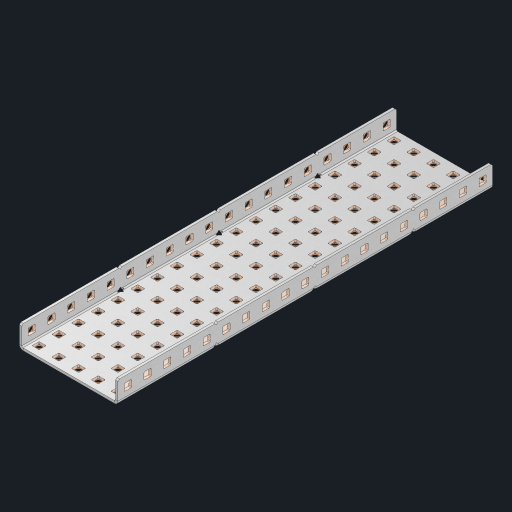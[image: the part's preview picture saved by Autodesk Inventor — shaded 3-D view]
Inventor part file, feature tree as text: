
AUTODESK INVENTOR PART (.ipt)
format: ipt  version: 2023 (Build 270158000, 158)  size: 1,603,072 bytes
history: native  units: in
note: dims shown in document units (in); Inventor stores cm internally (conversion verified against a paired STEP export)
features: other x138, extrude x132, sheet_metal_op x10, sketch x8, mirror x1, pattern_linear x1, chamfer x1
ambient origin geometry x8: Origin, YZ Plane, XZ Plane, XY Plane, X Axis, Y Axis, Z Axis, Center Point
bodies: Solid1 (feature_tree), Body (feature_tree)
feature tree (291):
  other  "Flange Pattern Plane"
  sheet_metal_op  "Flange Pattern"
  sheet_metal_op  "Body Pattern"
  other  "Arc Length"
  mirror  "Notch Mirror"
  pattern_linear  "Notch Pattern"  Spacing1=0.25in  [1 undecoded]
  chamfer  "End Chamfer"
  extrude  "Half Cut"  Depth=0.0625in
  sketch  "Sketch1"  dims[d0=2.5in]
  other  "Plate1"
  sketch  "Sketch2"  dims[d1=9.5in]
  other  "Plate2"
  sheet_metal_op  "Bend1"
  sheet_metal_op  "Corner1"
  sketch  "Sketch3"  dims[d2=0.0625in]
  other  "Flange Pattern Sketch"
  sketch  "Sketch7"  dims[d3=0.0625in]
  other  "Srf1"
  other  "Srf2"
  sketch  "Sketch8"  dims[d4=0.0312in]
  sketch  "Sketch9"  dims[d5=0.125in]
  other  "Srf91"
  sheet_metal_op  "Body Pattern Sketch"
  other  "Srf92"
  sketch  "Sketch13"  dims[d6=0.0625in]
  sketch  "Sketch14"  dims[d7=0.5in d8=90.0deg d9=0.0312in d10=0.25in d11=0.0625in d12=0.0625in d16=0.182in d17=0.02in d18=0.0625in d19=0.0in d20=0.25in d21=0.25in d46=0.172in d47=1.0in d48=0.0in d49=0.182in d50=0.02in d51=0.25in d52=0.25in d53=0.0625in d54=0.0in d55=0.172in d56=1.0in d57=0.0in d60=7.4803in d62=0.5in d63=1.9685in d65=0.5in d85=0.1473in d86=0.1782in d88=0.04in d89=0.0625in d90=0.0in d91=0.04in d92=0.0491in d95=2.5in d96=0.04in d97=0.25in d98=45.0deg d101=0.0in d102=2.497in d131=2.5in d132=7.4803in d134=0.5in d139=0.5in]
  other  "Srf856"
  other  "Srf1310"
  other  "Srf1311"
  other  "Srf1312"
  other  "Srf1376"
  other  "Srf1377"
  other  "Srf1728"
  other  "Srf1755"
  other  "Srf1878"
  other  "Srf1879"
  other  "Srf1880"
  other  "Srf1881"
  other  "Srf1882"
  other  "Srf1883"
  other  "Srf1884"
  other  "Srf1885"
  other  "Srf1886"
  other  "Srf1887"
  other  "Srf1888"
  other  "Srf1889"
  other  "Srf1890"
  other  "Srf1891"
  other  "Srf1892"
  other  "Srf1893"
  other  "Srf1894"
  other  "Srf1895"
  other  "Srf1896"
  other  "Srf1897"
  other  "Srf1898"
  other  "Srf1899"
  other  "Srf1900"
  other  "Srf1901"
  other  "Srf1902"
  other  "Srf1903"
  other  "Srf1904"
  other  "Srf1905"
  other  "Srf1906"
  other  "Srf1942"
  other  "Srf1943"
  other  "Srf1944"
  other  "Srf1945"
  other  "Srf1946"
  other  "Srf1947"
  other  "Srf1948"
  other  "Srf1949"
  other  "Srf1950"
  other  "Srf1951"
  other  "Srf1952"
  other  "Srf1953"
  other  "Srf1954"
  other  "Srf1955"
  other  "Srf1956"
  other  "Srf1957"
  other  "Srf1958"
  other  "Srf1959"
  other  "Srf1960"
  other  "Srf1961"
  other  "Srf1962"
  other  "Srf1963"
  other  "Srf1964"
  other  "Srf1965"
  other  "Srf1966"
  other  "Srf1967"
  other  "Srf1968"
  other  "Srf1969"
  other  "Srf1970"
  other  "Srf2111"
  other  "Srf2112"
  other  "Srf2113"
  other  "Srf2146"
  other  "Srf2147"
  other  "Srf2148"
  other  "Srf2149"
  other  "Srf2150"
  other  "Srf2151"
  other  "Srf2152"
  other  "Srf2153"
  other  "Srf2154"
  other  "Srf2155"
  other  "Srf2156"
  other  "Srf2157"
  other  "Srf2158"
  other  "Srf2159"
  other  "Srf2160"
  other  "Srf2161"
  other  "Srf2162"
  other  "Srf2163"
  other  "Srf2164"
  other  "Srf2165"
  other  "Srf2166"
  other  "Srf2167"
  other  "Srf2168"
  other  "Srf2169"
  other  "Srf2170"
  other  "Srf2171"
  other  "Srf2172"
  other  "Srf2173"
  other  "Srf2174"
  other  "Srf2175"
  other  "Srf2176"
  other  "Srf2177"
  other  "Srf2178"
  other  "Srf2179"
  other  "Srf2180"
  other  "Srf2181"
  other  "Srf2182"
  other  "Srf2183"
  other  "Srf2184"
  other  "Srf2185"
  other  "Srf2186"
  other  "Srf2187"
  other  "Srf2188"
  other  "Srf2189"
  other  "Srf2190"
  other  "Srf2191"
  other  "Srf2192"
  other  "Srf2193"
  other  "Srf2194"
  other  "Srf2195"
  other  "Srf2196"
  other  "Srf2197"
  other  "Srf2198"
  other  "Srf2199"
  other  "Srf2200"
  other  "Srf2201"
  other  "Srf2202"
  other  "Srf2203"
  other  "Srf2204"
  other  "Srf2205"
  sheet_metal_op  "Flange Stamp"
  sheet_metal_op  "Flange Circle"
  sheet_metal_op  "Body Stamp"
  sheet_metal_op  "Body Circle"
  sheet_metal_op  "Notch"
  extrude  "ExtrusionSrf2"  Depth=0.0625in
  extrude  "ExtrusionSrf92"  Depth=2.5in
  extrude  "ExtrusionSrf856"  Depth=0.02in
  extrude  "ExtrusionSrf1310"  Depth=0.0625in
  extrude  "ExtrusionSrf1311"  TaperAngle=0.0deg  [1 undecoded]
  extrude  "ExtrusionSrf1312"  Depth=0.25in
  extrude  "ExtrusionSrf1376"  Depth=0.25in
  extrude  "ExtrusionSrf1377"  Depth=2.5in
  extrude  "ExtrusionSrf1728"  Depth=2.5in TaperAngle=0.0deg
  extrude  "ExtrusionSrf1755"  Depth=2.5in
  extrude  "ExtrusionSrf1878"  Depth=0.02in
  extrude  "ExtrusionSrf1879"  Depth=0.25in
  extrude  "ExtrusionSrf1880"  Depth=0.25in
  extrude  "ExtrusionSrf1881"  Depth=0.0625in
  extrude  "ExtrusionSrf1882"  TaperAngle=0.0deg  [1 undecoded]
  extrude  "ExtrusionSrf1883"  Depth=2.5in
  extrude  "ExtrusionSrf1884"  Depth=2.5in TaperAngle=0.0deg
  extrude  "ExtrusionSrf1885"  Depth=2.5in
  extrude  "ExtrusionSrf1886"  Depth=2.5in
  extrude  "ExtrusionSrf1887"  Depth=2.5in
  extrude  "ExtrusionSrf1888"  Depth=2.5in
  extrude  "ExtrusionSrf1889"  Depth=2.5in
  extrude  "ExtrusionSrf1890"  Depth=0.0625in
  extrude  "ExtrusionSrf1891"  TaperAngle=0.0deg  [1 undecoded]
  extrude  "ExtrusionSrf1892"  Depth=2.5in
  extrude  "ExtrusionSrf1893"  Depth=2.5in
  extrude  "ExtrusionSrf1894"  Depth=2.5in
  extrude  "ExtrusionSrf1895"  Depth=0.25in TaperAngle=45.0deg
  extrude  "ExtrusionSrf1896"  TaperAngle=0.0deg  [1 undecoded]
  extrude  "ExtrusionSrf1897"  Depth=2.5in
  extrude  "ExtrusionSrf1898"  Depth=2.5in
  extrude  "ExtrusionSrf1899"  Depth=2.5in
  extrude  "ExtrusionSrf1900"  Depth=2.5in
  extrude  "ExtrusionSrf1901"  Depth=2.5in
  extrude  "ExtrusionSrf1902"  [1 undecoded]
  extrude  "ExtrusionSrf1903"  [1 undecoded]
  extrude  "ExtrusionSrf1904"  [1 undecoded]
  extrude  "ExtrusionSrf1905"  [1 undecoded]
  extrude  "ExtrusionSrf1906"  [1 undecoded]
  extrude  "ExtrusionSrf1942"  [1 undecoded]
  extrude  "ExtrusionSrf1943"  [1 undecoded]
  extrude  "ExtrusionSrf1944"  [1 undecoded]
  extrude  "ExtrusionSrf1945"  [1 undecoded]
  extrude  "ExtrusionSrf1946"  [1 undecoded]
  extrude  "ExtrusionSrf1947"  [1 undecoded]
  extrude  "ExtrusionSrf1948"  [1 undecoded]
  extrude  "ExtrusionSrf1949"  [1 undecoded]
  extrude  "ExtrusionSrf1950"  [1 undecoded]
  extrude  "ExtrusionSrf1951"  [1 undecoded]
  extrude  "ExtrusionSrf1952"  [1 undecoded]
  extrude  "ExtrusionSrf1953"  [1 undecoded]
  extrude  "ExtrusionSrf1954"  [1 undecoded]
  extrude  "ExtrusionSrf1955"  [1 undecoded]
  extrude  "ExtrusionSrf1956"  [1 undecoded]
  extrude  "ExtrusionSrf1957"  [1 undecoded]
  extrude  "ExtrusionSrf1958"  [1 undecoded]
  extrude  "ExtrusionSrf1959"  [1 undecoded]
  extrude  "ExtrusionSrf1960"  [1 undecoded]
  extrude  "ExtrusionSrf1961"  [1 undecoded]
  extrude  "ExtrusionSrf1962"  [1 undecoded]
  extrude  "ExtrusionSrf1963"  [1 undecoded]
  extrude  "ExtrusionSrf1964"  [1 undecoded]
  extrude  "ExtrusionSrf1965"  [1 undecoded]
  extrude  "ExtrusionSrf1966"  [1 undecoded]
  extrude  "ExtrusionSrf1967"  [1 undecoded]
  extrude  "ExtrusionSrf1968"  [1 undecoded]
  extrude  "ExtrusionSrf1969"  [1 undecoded]
  extrude  "ExtrusionSrf1970"  [1 undecoded]
  extrude  "ExtrusionSrf2111"  [1 undecoded]
  extrude  "ExtrusionSrf2112"  [1 undecoded]
  extrude  "ExtrusionSrf2113"  [1 undecoded]
  extrude  "ExtrusionSrf2146"  [1 undecoded]
  extrude  "ExtrusionSrf2147"  [1 undecoded]
  extrude  "ExtrusionSrf2148"  [1 undecoded]
  extrude  "ExtrusionSrf2149"  [1 undecoded]
  extrude  "ExtrusionSrf2150"  [1 undecoded]
  extrude  "ExtrusionSrf2151"  [1 undecoded]
  extrude  "ExtrusionSrf2152"  [1 undecoded]
  extrude  "ExtrusionSrf2153"  [1 undecoded]
  extrude  "ExtrusionSrf2154"  [1 undecoded]
  extrude  "ExtrusionSrf2155"  [1 undecoded]
  extrude  "ExtrusionSrf2156"  [1 undecoded]
  extrude  "ExtrusionSrf2157"  [1 undecoded]
  extrude  "ExtrusionSrf2158"  [1 undecoded]
  extrude  "ExtrusionSrf2159"  [1 undecoded]
  extrude  "ExtrusionSrf2160"  [1 undecoded]
  extrude  "ExtrusionSrf2161"  [1 undecoded]
  extrude  "ExtrusionSrf2162"  [1 undecoded]
  extrude  "ExtrusionSrf2163"  [1 undecoded]
  extrude  "ExtrusionSrf2164"  [1 undecoded]
  extrude  "ExtrusionSrf2165"  [1 undecoded]
  extrude  "ExtrusionSrf2166"  [1 undecoded]
  extrude  "ExtrusionSrf2167"  [1 undecoded]
  extrude  "ExtrusionSrf2168"  [1 undecoded]
  extrude  "ExtrusionSrf2169"  [1 undecoded]
  extrude  "ExtrusionSrf2170"  [1 undecoded]
  extrude  "ExtrusionSrf2171"  [1 undecoded]
  extrude  "ExtrusionSrf2172"  [1 undecoded]
  extrude  "ExtrusionSrf2173"  [1 undecoded]
  extrude  "ExtrusionSrf2174"  [1 undecoded]
  extrude  "ExtrusionSrf2175"  [1 undecoded]
  extrude  "ExtrusionSrf2176"  [1 undecoded]
  extrude  "ExtrusionSrf2177"  [1 undecoded]
  extrude  "ExtrusionSrf2178"  [1 undecoded]
  extrude  "ExtrusionSrf2179"  [1 undecoded]
  extrude  "ExtrusionSrf2180"  [1 undecoded]
  extrude  "ExtrusionSrf2181"  [1 undecoded]
  extrude  "ExtrusionSrf2182"  [1 undecoded]
  extrude  "ExtrusionSrf2183"  [1 undecoded]
  extrude  "ExtrusionSrf2184"  [1 undecoded]
  extrude  "ExtrusionSrf2185"  [1 undecoded]
  extrude  "ExtrusionSrf2186"  [1 undecoded]
  extrude  "ExtrusionSrf2187"  [1 undecoded]
  extrude  "ExtrusionSrf2188"  [1 undecoded]
  extrude  "ExtrusionSrf2189"  [1 undecoded]
  extrude  "ExtrusionSrf2190"  [1 undecoded]
  extrude  "ExtrusionSrf2191"  [1 undecoded]
  extrude  "ExtrusionSrf2192"  [1 undecoded]
  extrude  "ExtrusionSrf2193"  [1 undecoded]
  extrude  "ExtrusionSrf2194"  [1 undecoded]
  extrude  "ExtrusionSrf2195"  [1 undecoded]
  extrude  "ExtrusionSrf2196"  [1 undecoded]
  extrude  "ExtrusionSrf2197"  [1 undecoded]
  extrude  "ExtrusionSrf2198"  [1 undecoded]
  extrude  "ExtrusionSrf2199"  [1 undecoded]
  extrude  "ExtrusionSrf2200"  [1 undecoded]
  extrude  "ExtrusionSrf2201"  [1 undecoded]
  extrude  "ExtrusionSrf2202"  [1 undecoded]
  extrude  "ExtrusionSrf2203"  [1 undecoded]
  extrude  "ExtrusionSrf2204"  [1 undecoded]
  extrude  "ExtrusionSrf2205"  [1 undecoded]
note: 102 required parameter values undecoded (feature->parameter linkage not recoverable at this tier; creation-order binding heuristic only, values carry confidence <= 0.55)
